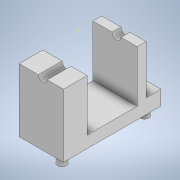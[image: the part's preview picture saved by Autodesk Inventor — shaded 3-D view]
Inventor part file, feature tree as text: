
AUTODESK INVENTOR PART (.ipt)
format: ipt  version: 2021 (Build 250183000, 183)  size: 144,384 bytes
history: native  units: mm
features: sketch x6, extrude x5
ambient origin geometry x8: Origin, YZ Plane, XZ Plane, XY Plane, X Axis, Y Axis, Z Axis, Center Point
bodies: Solid1 (feature_tree)
feature tree (11):
  extrude  "Extrusion1"  Depth=21.477mm
  extrude  "Extrusion2"  Depth=3.0mm
  extrude  "Extrusion3"  Depth=3.0mm
  extrude  "Extrusion4"  Depth=3.0mm
  sketch  "Sketch5"  dims[d9=3.0mm d10=3.0mm d11=0.0mm]
  extrude  "Extrusion5"  Depth=3.0mm TaperAngle=0.0deg
  sketch  "Sketch1"  dims[d0=33.0mm d1=21.477mm]
  sketch  "Sketch2"  dims[d2=15.0mm d3=0.0mm d4=3.0mm]
  sketch  "Sketch3"  dims[d5=2.5mm d6=3.0mm]
  sketch  "Sketch4"  dims[d7=28.0mm d8=3.0mm]
  sketch  "Sketch6"  dims[d12=8.0mm d13=8.0mm d14=20.0mm d15=0.0mm d16=0.0mm d17=3.0mm d18=6.983mm d19=0.0mm d20=0.0mm d21=5.0mm d22=5.0mm d23=0.0mm]
